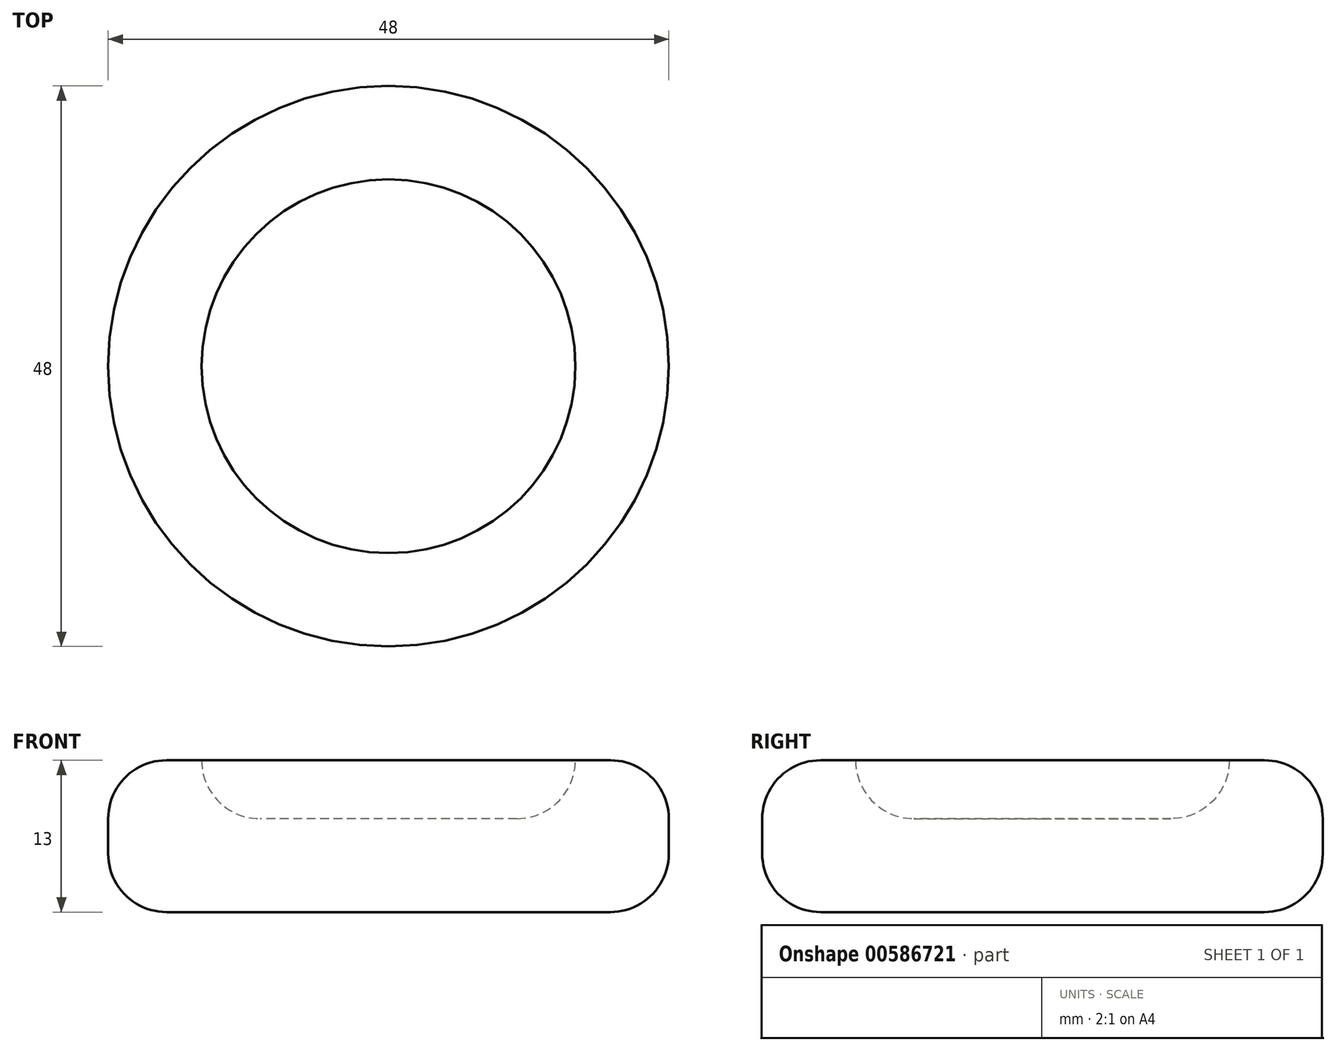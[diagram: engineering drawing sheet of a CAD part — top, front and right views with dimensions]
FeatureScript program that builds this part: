
annotation { "Feature Type Name" : "Feature", "Feature Type Description" : "" }
export const myFeature = defineFeature(function(context is Context, id is Id, definition is map)
    precondition{}
    {
        {
            var Q0;
            Q0=qCreatedBy(makeId("Top.planeOp"),FACE);
            var sketch = newSketch(context, id + "F0", { "sketchPlane" : qUnion([Q0])});
            skCircle(sketch, "E0", {"center": v(-3.01, 6.39) * mm, "radius": 16 * mm});
            skSolve(sketch);
        }
        {
            var Q0;
            Q0=makeQuery(id+"F0.imprint","IMPRINT",FACE,{"disambiguationData":[TD([[makeQuery(id+"F0.imprint","IMPRINT",EDGE,{"derivedFrom":sQuery(id+"F0.wireOp",EDGE,"E0")}),1.0]])]});
            extrude(context, id + "F1", {"entities" : qUnion([Q0]), "depth" : 5 * mm, "offsetDistance" : 25 * mm});
        }
        {
            var Q0;
            Q0=makeQuery(id+"F1.opExtrude","CAP_FACE",FACE,{"disambiguationData":[OSD([sQuery(id+"F0.wireOp",EDGE,"E0")])],"isStart":false});
            shell(context, id + "F2", {"entities" : qUnion([Q0]), "thickness" : 8 * mm, "oppositeDirection" : true});
        }
        {
            var Q0;
            Q0=makeQuery(id+"F1.opExtrude","CAP_EDGE",EDGE,{"disambiguationData":[OSD([sQuery(id+"F0.wireOp",EDGE,"E0")])],"isStart":false});
            fillet(context, id + "F3", {"entities" : qUnion([Q0]), "radius" : 5 * mm, "tangentPropagation" : true, "allowEdgeOverflow" : false});
        }
        {
            var Q0;
            Q0=makeQuery(id+"F1.opExtrude","CAP_EDGE",EDGE,{"disambiguationData":[OSD([sQuery(id+"F0.wireOp",EDGE,"E0")])],"isStart":true});
            fillet(context, id + "F4", {"entities" : qUnion([Q0]), "radius" : 5 * mm, "tangentPropagation" : true, "allowEdgeOverflow" : false});
        }
        {
            var Q0;
            {var subQ0=sQuery(id+"F0.wireOp",EDGE,"E0");Q0=makeQuery(id+"F2.opShell","OFFSET_FACE",FACE,{"disambiguationData":[OSD([subQ0]),TDD([makeQuery(id+"F1.opExtrude","CAP_FACE",FACE,{"disambiguationData":[OSD([subQ0])],"isStart":true})])]});}
            fillet(context, id + "F5", {"entities" : qUnion([Q0]), "radius" : 5 * mm, "tangentPropagation" : true, "allowEdgeOverflow" : false});
        }
    });
